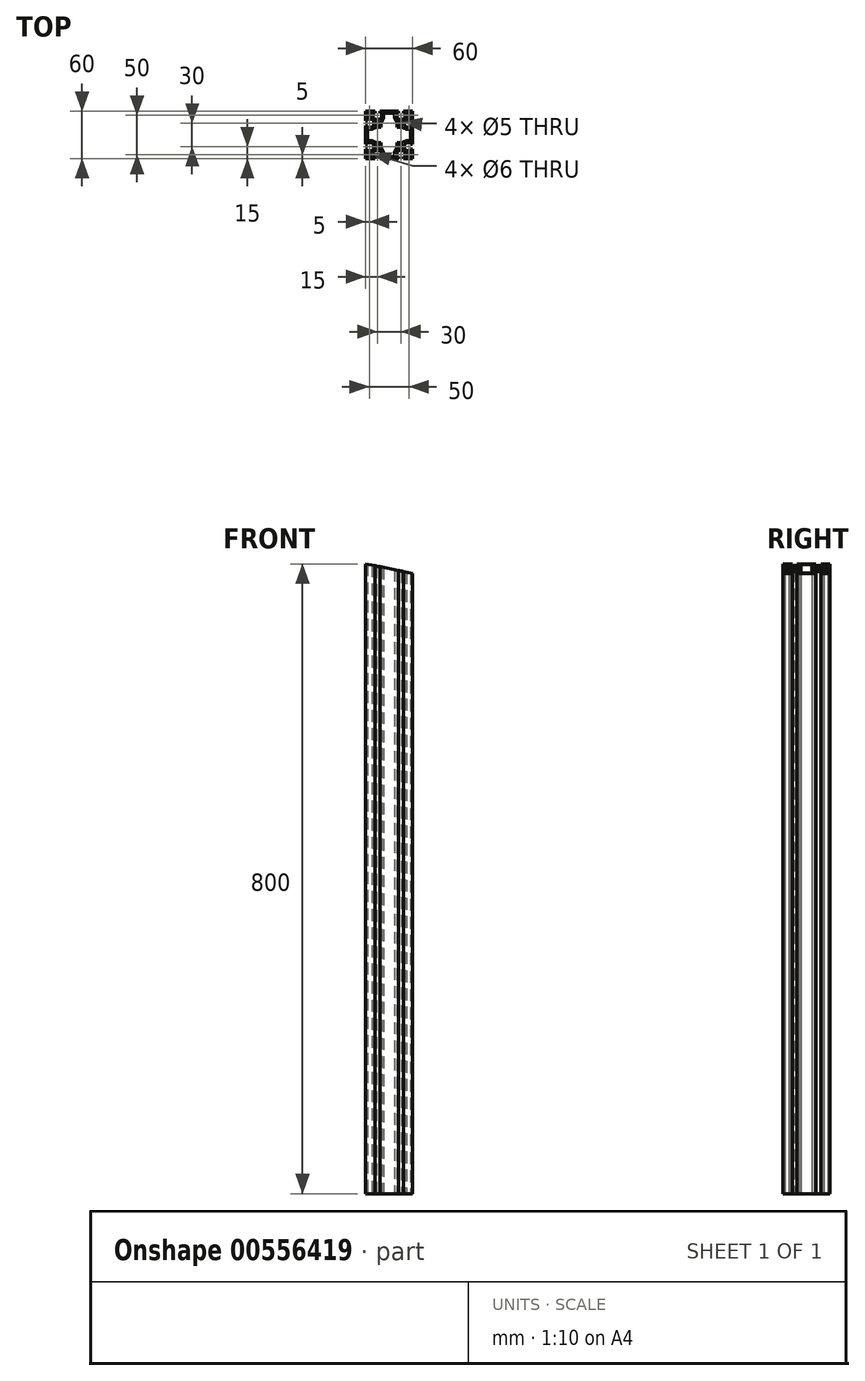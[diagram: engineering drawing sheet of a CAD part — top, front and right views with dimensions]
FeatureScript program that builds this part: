
annotation { "Feature Type Name" : "Feature", "Feature Type Description" : "" }
export const myFeature = defineFeature(function(context is Context, id is Id, definition is map)
    precondition{}
    {
        {
            var Q0;
            Q0=qCreatedBy(makeId("Top.planeOp"),FACE);
            var sketch = newSketch(context, id + "F0", { "sketchPlane" : qUnion([Q0])});
            skLineSegment(sketch, "E0.bottom", {"start": v(30, -30) * mm, "end": v(-30, -30) * mm});
            skLineSegment(sketch, "E0.top", {"start": v(30, 30) * mm, "end": v(-30, 30) * mm});
            skLineSegment(sketch, "E0.left", {"start": v(30, -30) * mm, "end": v(30, 30) * mm});
            skLineSegment(sketch, "E0.right", {"start": v(-30, -30) * mm, "end": v(-30, 30) * mm});
            skPoint(sketch, "E0.middle", {"position": v(0, 0) * mm});
            skLineSegment(sketch, "E1.top", {"start": v(-11.85, 30) * mm, "end": v(-18.15, 30) * mm});
            skLineSegment(sketch, "E1.left", {"start": v(-11.85, 27.5) * mm, "end": v(-11.85, 30) * mm});
            skLineSegment(sketch, "E1.right", {"start": v(-18.15, 27.5) * mm, "end": v(-18.15, 30) * mm});
            skPoint(sketch, "E1.middle", {"position": v(-15, 28.75) * mm});
            skLineSegment(sketch, "E2.bottom", {"start": v(-9.85, 27.5) * mm, "end": v(-11.85, 27.5) * mm});
            skLineSegment(sketch, "E2.left", {"start": v(-9.85, 27.5) * mm, "end": v(-9.85, 21.55) * mm});
            skLineSegment(sketch, "E2.right", {"start": v(-20.15, 27.5) * mm, "end": v(-20.15, 21.55) * mm});
            skPoint(sketch, "E2.middle", {"position": v(-15, 24.52) * mm});
            skArc(sketch, "E3", {"start": v(-20.15, 21.55) * mm, "mid": v(-15, 19.5) * mm, "end": v(-9.85, 21.55) * mm});
            skPoint(sketch, "E4.MirrorP", {"position": v(15, 24.52) * mm});
            skPoint(sketch, "E5.MirrorP", {"position": v(15, 28.75) * mm});
            skLineSegment(sketch, "E6.MirrorCS", {"start": v(11.85, 27.5) * mm, "end": v(11.85, 30) * mm});
            skLineSegment(sketch, "E7.MirrorCS", {"start": v(18.15, 27.5) * mm, "end": v(18.15, 30) * mm});
            skLineSegment(sketch, "E8.MirrorCS", {"start": v(9.85, 27.5) * mm, "end": v(11.85, 27.5) * mm});
            skLineSegment(sketch, "E9.MirrorCS", {"start": v(9.85, 27.5) * mm, "end": v(9.85, 21.55) * mm});
            skArc(sketch, "E10.MirrorCS", {"start": v(20.15, 21.55) * mm, "mid": v(15, 19.5) * mm, "end": v(9.85, 21.55) * mm});
            skLineSegment(sketch, "E11.MirrorCS", {"start": v(20.15, 27.5) * mm, "end": v(20.15, 21.55) * mm});
            skLineSegment(sketch, "E12.MirrorCS", {"start": v(11.85, 30) * mm, "end": v(18.15, 30) * mm});
            skLineSegment(sketch, "E13.1.0", {"start": v(27.5, 20.15) * mm, "end": v(21.55, 20.15) * mm});
            skLineSegment(sketch, "E13.1.1", {"start": v(27.5, 9.85) * mm, "end": v(21.55, 9.85) * mm});
            skArc(sketch, "E13.1.2", {"start": v(21.55, 20.15) * mm, "mid": v(19.5, 15) * mm, "end": v(21.55, 9.85) * mm});
            skLineSegment(sketch, "E13.1.3", {"start": v(27.5, -9.85) * mm, "end": v(21.55, -9.85) * mm});
            skLineSegment(sketch, "E13.1.4", {"start": v(27.5, -20.15) * mm, "end": v(21.55, -20.15) * mm});
            skPoint(sketch, "E13.1.5", {"position": v(28.75, 15) * mm});
            skPoint(sketch, "E13.1.6", {"position": v(28.75, -15) * mm});
            skArc(sketch, "E13.1.7", {"start": v(21.55, -20.15) * mm, "mid": v(19.5, -15) * mm, "end": v(21.55, -9.85) * mm});
            skPoint(sketch, "E13.1.8", {"position": v(24.52, -15) * mm});
            skPoint(sketch, "E13.1.9", {"position": v(24.52, 15) * mm});
            skLineSegment(sketch, "E13.1.10", {"start": v(27.5, 9.85) * mm, "end": v(27.5, 20.15) * mm});
            skLineSegment(sketch, "E13.1.11", {"start": v(27.5, -11.85) * mm, "end": v(27.5, -18.15) * mm});
            skLineSegment(sketch, "E13.1.12", {"start": v(30, 11.85) * mm, "end": v(30, 18.15) * mm});
            skLineSegment(sketch, "E13.1.13", {"start": v(30, -11.85) * mm, "end": v(30, -18.15) * mm});
            skLineSegment(sketch, "E13.1.14", {"start": v(27.5, 18.15) * mm, "end": v(30, 18.15) * mm});
            skLineSegment(sketch, "E13.1.15", {"start": v(27.5, 11.85) * mm, "end": v(30, 11.85) * mm});
            skLineSegment(sketch, "E13.1.16", {"start": v(27.5, 11.85) * mm, "end": v(27.5, 18.15) * mm});
            skLineSegment(sketch, "E13.1.17", {"start": v(27.5, -9.85) * mm, "end": v(27.5, -20.15) * mm});
            skLineSegment(sketch, "E13.1.18", {"start": v(27.5, -18.15) * mm, "end": v(30, -18.15) * mm});
            skLineSegment(sketch, "E13.1.19", {"start": v(27.5, -11.85) * mm, "end": v(30, -11.85) * mm});
            skLineSegment(sketch, "E13.2.0", {"start": v(20.15, -27.5) * mm, "end": v(20.15, -21.55) * mm});
            skLineSegment(sketch, "E13.2.1", {"start": v(9.85, -27.5) * mm, "end": v(9.85, -21.55) * mm});
            skArc(sketch, "E13.2.2", {"start": v(20.15, -21.55) * mm, "mid": v(15, -19.5) * mm, "end": v(9.85, -21.55) * mm});
            skLineSegment(sketch, "E13.2.3", {"start": v(-9.85, -27.5) * mm, "end": v(-9.85, -21.55) * mm});
            skLineSegment(sketch, "E13.2.4", {"start": v(-20.15, -27.5) * mm, "end": v(-20.15, -21.55) * mm});
            skPoint(sketch, "E13.2.5", {"position": v(15, -28.75) * mm});
            skPoint(sketch, "E13.2.6", {"position": v(-15, -28.75) * mm});
            skArc(sketch, "E13.2.7", {"start": v(-20.15, -21.55) * mm, "mid": v(-15, -19.5) * mm, "end": v(-9.85, -21.55) * mm});
            skPoint(sketch, "E13.2.8", {"position": v(-15, -24.52) * mm});
            skPoint(sketch, "E13.2.9", {"position": v(15, -24.52) * mm});
            skLineSegment(sketch, "E13.2.10", {"start": v(9.85, -27.5) * mm, "end": v(20.15, -27.5) * mm});
            skLineSegment(sketch, "E13.2.11", {"start": v(-11.85, -27.5) * mm, "end": v(-18.15, -27.5) * mm});
            skLineSegment(sketch, "E13.2.12", {"start": v(11.85, -30) * mm, "end": v(18.15, -30) * mm});
            skLineSegment(sketch, "E13.2.13", {"start": v(-11.85, -30) * mm, "end": v(-18.15, -30) * mm});
            skLineSegment(sketch, "E13.2.14", {"start": v(18.15, -27.5) * mm, "end": v(18.15, -30) * mm});
            skLineSegment(sketch, "E13.2.15", {"start": v(11.85, -27.5) * mm, "end": v(11.85, -30) * mm});
            skLineSegment(sketch, "E13.2.16", {"start": v(11.85, -27.5) * mm, "end": v(18.15, -27.5) * mm});
            skLineSegment(sketch, "E13.2.17", {"start": v(-9.85, -27.5) * mm, "end": v(-20.15, -27.5) * mm});
            skLineSegment(sketch, "E13.2.18", {"start": v(-18.15, -27.5) * mm, "end": v(-18.15, -30) * mm});
            skLineSegment(sketch, "E13.2.19", {"start": v(-11.85, -27.5) * mm, "end": v(-11.85, -30) * mm});
            skLineSegment(sketch, "E13.3.0", {"start": v(-27.5, -20.15) * mm, "end": v(-21.55, -20.15) * mm});
            skLineSegment(sketch, "E13.3.1", {"start": v(-27.5, -9.85) * mm, "end": v(-21.55, -9.85) * mm});
            skArc(sketch, "E13.3.2", {"start": v(-21.55, -20.15) * mm, "mid": v(-19.5, -15) * mm, "end": v(-21.55, -9.85) * mm});
            skLineSegment(sketch, "E13.3.3", {"start": v(-27.5, 9.85) * mm, "end": v(-21.55, 9.85) * mm});
            skLineSegment(sketch, "E13.3.4", {"start": v(-27.5, 20.15) * mm, "end": v(-21.55, 20.15) * mm});
            skPoint(sketch, "E13.3.5", {"position": v(-28.75, -15) * mm});
            skPoint(sketch, "E13.3.6", {"position": v(-28.75, 15) * mm});
            skArc(sketch, "E13.3.7", {"start": v(-21.55, 20.15) * mm, "mid": v(-19.5, 15) * mm, "end": v(-21.55, 9.85) * mm});
            skPoint(sketch, "E13.3.8", {"position": v(-24.52, 15) * mm});
            skPoint(sketch, "E13.3.9", {"position": v(-24.52, -15) * mm});
            skLineSegment(sketch, "E13.3.10", {"start": v(-27.5, -9.85) * mm, "end": v(-27.5, -20.15) * mm});
            skLineSegment(sketch, "E13.3.11", {"start": v(-27.5, 11.85) * mm, "end": v(-27.5, 18.15) * mm});
            skLineSegment(sketch, "E13.3.12", {"start": v(-30, -11.85) * mm, "end": v(-30, -18.15) * mm});
            skLineSegment(sketch, "E13.3.13", {"start": v(-30, 11.85) * mm, "end": v(-30, 18.15) * mm});
            skLineSegment(sketch, "E13.3.14", {"start": v(-27.5, -18.15) * mm, "end": v(-30, -18.15) * mm});
            skLineSegment(sketch, "E13.3.15", {"start": v(-27.5, -11.85) * mm, "end": v(-30, -11.85) * mm});
            skLineSegment(sketch, "E13.3.16", {"start": v(-27.5, -11.85) * mm, "end": v(-27.5, -18.15) * mm});
            skLineSegment(sketch, "E13.3.17", {"start": v(-27.5, 9.85) * mm, "end": v(-27.5, 20.15) * mm});
            skLineSegment(sketch, "E13.3.18", {"start": v(-27.5, 18.15) * mm, "end": v(-30, 18.15) * mm});
            skLineSegment(sketch, "E13.3.19", {"start": v(-27.5, 11.85) * mm, "end": v(-30, 11.85) * mm});
            skLineSegment(sketch, "E13.anchor1", {"start": v(0, 0) * mm, "end": v(-20.15, 21.55) * mm, "construction": true});
            skLineSegment(sketch, "E13.anchor2", {"start": v(0, 0) * mm, "end": v(-21.55, -20.15) * mm, "construction": true});
            skLineSegment(sketch, "E14.trimOffspring", {"start": v(-18.15, 27.5) * mm, "end": v(-20.15, 27.5) * mm});
            skLineSegment(sketch, "E15.trimOffspring", {"start": v(18.15, 27.5) * mm, "end": v(20.15, 27.5) * mm});
            skCircle(sketch, "E16", {"center": v(-15, 15) * mm, "radius": 2.5 * mm});
            skCircle(sketch, "E17", {"center": v(-25, 25) * mm, "radius": 3 * mm});
            skCircle(sketch, "E18.MirrorC", {"center": v(25, 25) * mm, "radius": 3 * mm});
            skCircle(sketch, "E19.MirrorC", {"center": v(25, -25) * mm, "radius": 3 * mm});
            skCircle(sketch, "E20.MirrorC", {"center": v(-25, -25) * mm, "radius": 3 * mm});
            skCircle(sketch, "E21.MirrorC", {"center": v(15, 15) * mm, "radius": 2.5 * mm});
            skCircle(sketch, "E22.MirrorC", {"center": v(15, -15) * mm, "radius": 2.5 * mm});
            skCircle(sketch, "E23.MirrorC", {"center": v(-15, -15) * mm, "radius": 2.5 * mm});
            skLineSegment(sketch, "E24", {"start": v(-7, 27.5) * mm, "end": v(0, 27.5) * mm});
            skLineSegment(sketch, "E25", {"start": v(-7, 27.5) * mm, "end": v(-7, 22) * mm});
            skLineSegment(sketch, "E26", {"start": v(-10, 10) * mm, "end": v(-10, 16) * mm});
            skLineSegment(sketch, "E27", {"start": v(-10, 16) * mm, "end": v(-7, 22) * mm});
            skLineSegment(sketch, "E28.MirrorCS", {"start": v(10, 10) * mm, "end": v(10, 16) * mm});
            skLineSegment(sketch, "E29.MirrorCS", {"start": v(10, 16) * mm, "end": v(7, 22) * mm});
            skLineSegment(sketch, "E30.MirrorCS", {"start": v(7, 27.5) * mm, "end": v(0, 27.5) * mm});
            skLineSegment(sketch, "E31.MirrorCS", {"start": v(7, 27.5) * mm, "end": v(7, 22) * mm});
            skLineSegment(sketch, "E32.1.0", {"start": v(-10, -10) * mm, "end": v(-16, -10) * mm});
            skLineSegment(sketch, "E32.1.1", {"start": v(-16, -10) * mm, "end": v(-22, -7) * mm});
            skLineSegment(sketch, "E32.1.2", {"start": v(-27.5, -7) * mm, "end": v(-22, -7) * mm});
            skLineSegment(sketch, "E32.1.3", {"start": v(-27.5, -7) * mm, "end": v(-27.5, 0) * mm});
            skLineSegment(sketch, "E32.1.4", {"start": v(-27.5, 7) * mm, "end": v(-27.5, 0) * mm});
            skLineSegment(sketch, "E32.1.5", {"start": v(-27.5, 7) * mm, "end": v(-22, 7) * mm});
            skLineSegment(sketch, "E32.1.6", {"start": v(-16, 10) * mm, "end": v(-22, 7) * mm});
            skLineSegment(sketch, "E32.1.7", {"start": v(-10, 10) * mm, "end": v(-16, 10) * mm});
            skLineSegment(sketch, "E32.2.0", {"start": v(10, -10) * mm, "end": v(10, -16) * mm});
            skLineSegment(sketch, "E32.2.1", {"start": v(10, -16) * mm, "end": v(7, -22) * mm});
            skLineSegment(sketch, "E32.2.2", {"start": v(7, -27.5) * mm, "end": v(7, -22) * mm});
            skLineSegment(sketch, "E32.2.3", {"start": v(7, -27.5) * mm, "end": v(0, -27.5) * mm});
            skLineSegment(sketch, "E32.2.4", {"start": v(-7, -27.5) * mm, "end": v(0, -27.5) * mm});
            skLineSegment(sketch, "E32.2.5", {"start": v(-7, -27.5) * mm, "end": v(-7, -22) * mm});
            skLineSegment(sketch, "E32.2.6", {"start": v(-10, -16) * mm, "end": v(-7, -22) * mm});
            skLineSegment(sketch, "E32.2.7", {"start": v(-10, -10) * mm, "end": v(-10, -16) * mm});
            skLineSegment(sketch, "E32.3.0", {"start": v(10, 10) * mm, "end": v(16, 10) * mm});
            skLineSegment(sketch, "E32.3.1", {"start": v(16, 10) * mm, "end": v(22, 7) * mm});
            skLineSegment(sketch, "E32.3.2", {"start": v(27.5, 7) * mm, "end": v(22, 7) * mm});
            skLineSegment(sketch, "E32.3.3", {"start": v(27.5, 7) * mm, "end": v(27.5, 0) * mm});
            skLineSegment(sketch, "E32.3.4", {"start": v(27.5, -7) * mm, "end": v(27.5, 0) * mm});
            skLineSegment(sketch, "E32.3.5", {"start": v(27.5, -7) * mm, "end": v(22, -7) * mm});
            skLineSegment(sketch, "E32.3.6", {"start": v(16, -10) * mm, "end": v(22, -7) * mm});
            skLineSegment(sketch, "E32.3.7", {"start": v(10, -10) * mm, "end": v(16, -10) * mm});
            skSolve(sketch);
        }
        {
            var Q0;
            {var subQ30=sQuery(id+"F0.wireOp",EDGE,"E1.left");Q0=makeQuery(id+"F0.imprint","IMPRINT",FACE,{"disambiguationData":[TD([[makeQuery(id+"F0.imprint","IMPRINT",EDGE,{"derivedFrom":subQ30}),-1.0]])]});}
            extrude(context, id + "F1", {"entities" : qUnion([Q0]), "depth" : 800 * mm, "offsetDistance" : 25 * mm});
        }
        {
            var Q0;
            Q0=makeQuery(id+"F1.opExtrude","SWEPT_EDGE",EDGE,{"disambiguationData":[OSD([sQuery(id+"F0.wireOp",EDGE,"E24"),sQuery(id+"F0.wireOp",EDGE,"E25")])]});
            var Q1;
            Q1=makeQuery(id+"F1.opExtrude","SWEPT_EDGE",EDGE,{"disambiguationData":[OSD([sQuery(id+"F0.wireOp",EDGE,"E30.MirrorCS"),sQuery(id+"F0.wireOp",EDGE,"E31.MirrorCS")])]});
            var Q2;
            Q2=makeQuery(id+"F1.opExtrude","SWEPT_EDGE",EDGE,{"disambiguationData":[OSD([sQuery(id+"F0.wireOp",EDGE,"840db5bc-c403-45cd-90c7-254e62d9e8c5.3.2"),sQuery(id+"F0.wireOp",EDGE,"840db5bc-c403-45cd-90c7-254e62d9e8c5.3.3")])]});
            var Q3;
            Q3=makeQuery(id+"F1.opExtrude","SWEPT_EDGE",EDGE,{"disambiguationData":[OSD([sQuery(id+"F0.wireOp",EDGE,"840db5bc-c403-45cd-90c7-254e62d9e8c5.3.4"),sQuery(id+"F0.wireOp",EDGE,"840db5bc-c403-45cd-90c7-254e62d9e8c5.3.5")])]});
            var Q4;
            Q4=makeQuery(id+"F1.opExtrude","SWEPT_EDGE",EDGE,{"disambiguationData":[OSD([sQuery(id+"F0.wireOp",EDGE,"840db5bc-c403-45cd-90c7-254e62d9e8c5.1.4"),sQuery(id+"F0.wireOp",EDGE,"840db5bc-c403-45cd-90c7-254e62d9e8c5.1.5")])]});
            var Q5;
            Q5=makeQuery(id+"F1.opExtrude","SWEPT_EDGE",EDGE,{"disambiguationData":[OSD([sQuery(id+"F0.wireOp",EDGE,"840db5bc-c403-45cd-90c7-254e62d9e8c5.1.2"),sQuery(id+"F0.wireOp",EDGE,"840db5bc-c403-45cd-90c7-254e62d9e8c5.1.3")])]});
            var Q6;
            Q6=makeQuery(id+"F1.opExtrude","SWEPT_EDGE",EDGE,{"disambiguationData":[OSD([sQuery(id+"F0.wireOp",EDGE,"840db5bc-c403-45cd-90c7-254e62d9e8c5.2.2"),sQuery(id+"F0.wireOp",EDGE,"840db5bc-c403-45cd-90c7-254e62d9e8c5.2.3")])]});
            var Q7;
            Q7=makeQuery(id+"F1.opExtrude","SWEPT_EDGE",EDGE,{"disambiguationData":[OSD([sQuery(id+"F0.wireOp",EDGE,"840db5bc-c403-45cd-90c7-254e62d9e8c5.2.4"),sQuery(id+"F0.wireOp",EDGE,"840db5bc-c403-45cd-90c7-254e62d9e8c5.2.5")])]});
            fillet(context, id + "F2", {"entities" : qUnion([Q0, Q1, Q2, Q3, Q4, Q5, Q6, Q7]), "radius" : 2 * mm, "tangentPropagation" : true, "allowEdgeOverflow" : false});
        }
        {
            var Q0;
            Q0=makeQuery(id+"F1.opExtrude","SWEPT_EDGE",EDGE,{"disambiguationData":[OSD([sQuery(id+"F0.wireOp",EDGE,"E26"),sQuery(id+"F0.wireOp",EDGE,"E27")])]});
            var Q1;
            Q1=makeQuery(id+"F1.opExtrude","SWEPT_EDGE",EDGE,{"disambiguationData":[OSD([sQuery(id+"F0.wireOp",EDGE,"E28.MirrorCS"),sQuery(id+"F0.wireOp",EDGE,"E29.MirrorCS")])]});
            var Q2;
            Q2=makeQuery(id+"F1.opExtrude","SWEPT_EDGE",EDGE,{"disambiguationData":[OSD([sQuery(id+"F0.wireOp",EDGE,"840db5bc-c403-45cd-90c7-254e62d9e8c5.3.0"),sQuery(id+"F0.wireOp",EDGE,"840db5bc-c403-45cd-90c7-254e62d9e8c5.3.1")])]});
            var Q3;
            Q3=makeQuery(id+"F1.opExtrude","SWEPT_EDGE",EDGE,{"disambiguationData":[OSD([sQuery(id+"F0.wireOp",EDGE,"840db5bc-c403-45cd-90c7-254e62d9e8c5.1.6"),sQuery(id+"F0.wireOp",EDGE,"840db5bc-c403-45cd-90c7-254e62d9e8c5.1.7")])]});
            var Q4;
            Q4=makeQuery(id+"F1.opExtrude","SWEPT_EDGE",EDGE,{"disambiguationData":[OSD([sQuery(id+"F0.wireOp",EDGE,"840db5bc-c403-45cd-90c7-254e62d9e8c5.1.0"),sQuery(id+"F0.wireOp",EDGE,"840db5bc-c403-45cd-90c7-254e62d9e8c5.1.1")])]});
            var Q5;
            Q5=makeQuery(id+"F1.opExtrude","SWEPT_EDGE",EDGE,{"disambiguationData":[OSD([sQuery(id+"F0.wireOp",EDGE,"840db5bc-c403-45cd-90c7-254e62d9e8c5.3.6"),sQuery(id+"F0.wireOp",EDGE,"840db5bc-c403-45cd-90c7-254e62d9e8c5.3.7")])]});
            var Q6;
            Q6=makeQuery(id+"F1.opExtrude","SWEPT_EDGE",EDGE,{"disambiguationData":[OSD([sQuery(id+"F0.wireOp",EDGE,"840db5bc-c403-45cd-90c7-254e62d9e8c5.2.0"),sQuery(id+"F0.wireOp",EDGE,"840db5bc-c403-45cd-90c7-254e62d9e8c5.2.1")])]});
            var Q7;
            Q7=makeQuery(id+"F1.opExtrude","SWEPT_EDGE",EDGE,{"disambiguationData":[OSD([sQuery(id+"F0.wireOp",EDGE,"840db5bc-c403-45cd-90c7-254e62d9e8c5.2.6"),sQuery(id+"F0.wireOp",EDGE,"840db5bc-c403-45cd-90c7-254e62d9e8c5.2.7")])]});
            fillet(context, id + "F3", {"entities" : qUnion([Q0, Q1, Q2, Q3, Q4, Q5, Q6, Q7]), "radius" : 7 * mm, "tangentPropagation" : true, "allowEdgeOverflow" : false});
        }
        {
            var Q0;
            {var subQ0=sQuery(id+"F0.wireOp",EDGE,"E0.bottom");Q0=makeQuery(id+"F1.opExtrude","SWEPT_FACE",FACE,{"disambiguationData":[OSD([subQ0]),TDD([makeQuery(id+"F0.imprint","IMPRINT",EDGE,{"disambiguationData":[TD([[makeQuery(id+"F0.imprint","INTERSECT",VERTEX,{"derivedFrom":[subQ0,sQuery(id+"F0.wireOp",EDGE,"E13.2.12"),sQuery(id+"F0.wireOp",EDGE,"E13.2.15")]}),-1.0]])],"derivedFrom":subQ0})])]});}
            var sketch = newSketch(context, id + "F4", { "sketchPlane" : qUnion([Q0])});
            skLineSegment(sketch, "E33.0", {"start": v(-18.15, 800) * mm, "end": v(-30, 800) * mm});
            skLineSegment(sketch, "E33.1", {"start": v(30, 800) * mm, "end": v(30, 0) * mm});
            skLineSegment(sketch, "E34", {"start": v(-30, 800) * mm, "end": v(30, 800) * mm});
            skLineSegment(sketch, "E35", {"start": v(30, 740) * mm, "end": v(-30, 800) * mm});
            skLineSegment(sketch, "E36.0", {"start": v(-18.15, 0) * mm, "end": v(-30, 0) * mm});
            skLineSegment(sketch, "E37", {"start": v(-30, 0) * mm, "end": v(30, 0) * mm});
            skLineSegment(sketch, "E38", {"start": v(30, 60) * mm, "end": v(-30, 0) * mm});
            skSolve(sketch);
        }
        {
            var Q0;
            Q0=qCreatedBy(makeId("Front.planeOp"),FACE);
            var sketch = newSketch(context, id + "F5", { "sketchPlane" : qUnion([Q0])});
            skLineSegment(sketch, "E39.bottom", {"start": v(113.94, 882.4) * mm, "end": v(-8.75, 906.81) * mm});
            skLineSegment(sketch, "E39.top", {"start": v(92.7, 775.6) * mm, "end": v(-30, 800) * mm});
            skLineSegment(sketch, "E39.left", {"start": v(113.94, 882.4) * mm, "end": v(92.7, 775.6) * mm});
            skLineSegment(sketch, "E39.right", {"start": v(-8.75, 906.81) * mm, "end": v(-30, 800) * mm});
            skSolve(sketch);
        }
        {
            var Q0;
            Q0=qSketchRegion(id+"F5",true);
            extrude(context, id + "F6", {"entities" : qUnion([Q0]), "operationType" : NewBodyOperationType.REMOVE, "depth" : 30 * mm, "offsetDistance" : 25 * mm, "hasSecondDirection" : true, "secondDirectionOppositeDirection" : true, "secondDirectionDepth" : 30 * mm});
        }
    });
